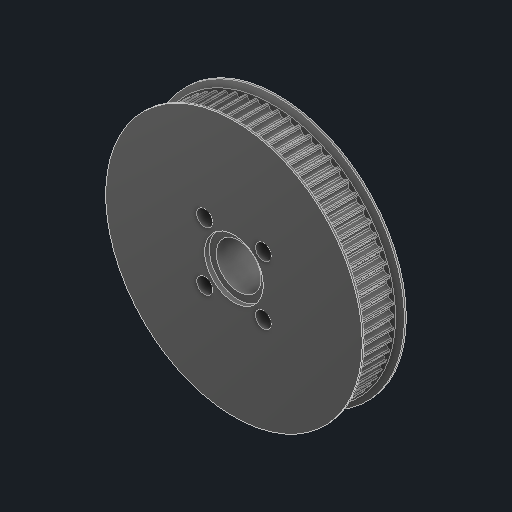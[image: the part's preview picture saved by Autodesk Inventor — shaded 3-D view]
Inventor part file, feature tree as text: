
AUTODESK INVENTOR PART (.ipt)
format: ipt  version: 2024.2 (Build 282272000, 272)  size: 1,394,176 bytes
history: native  units: in
note: dims shown in document units (in); Inventor stores cm internally (conversion verified against a paired STEP export)
features: other x2, extrude x1, sketch x1
ambient origin geometry x8: Origin, YZ Plane, XZ Plane, XY Plane, X Axis, Y Axis, Z Axis, Center Point
bodies: Body1 (feature_tree)
feature tree (4):
  other  "Thin_70T.step"
  extrude  "Extrusion4"  Depth=0.315in
  sketch  "Sketch5"  dims[d13=0.315in d14=0.315in d15=0.315in d16=0.315in d17=0.0984in d18=0.0in]
  other  "[LS] Pulley HTD3 70T"
